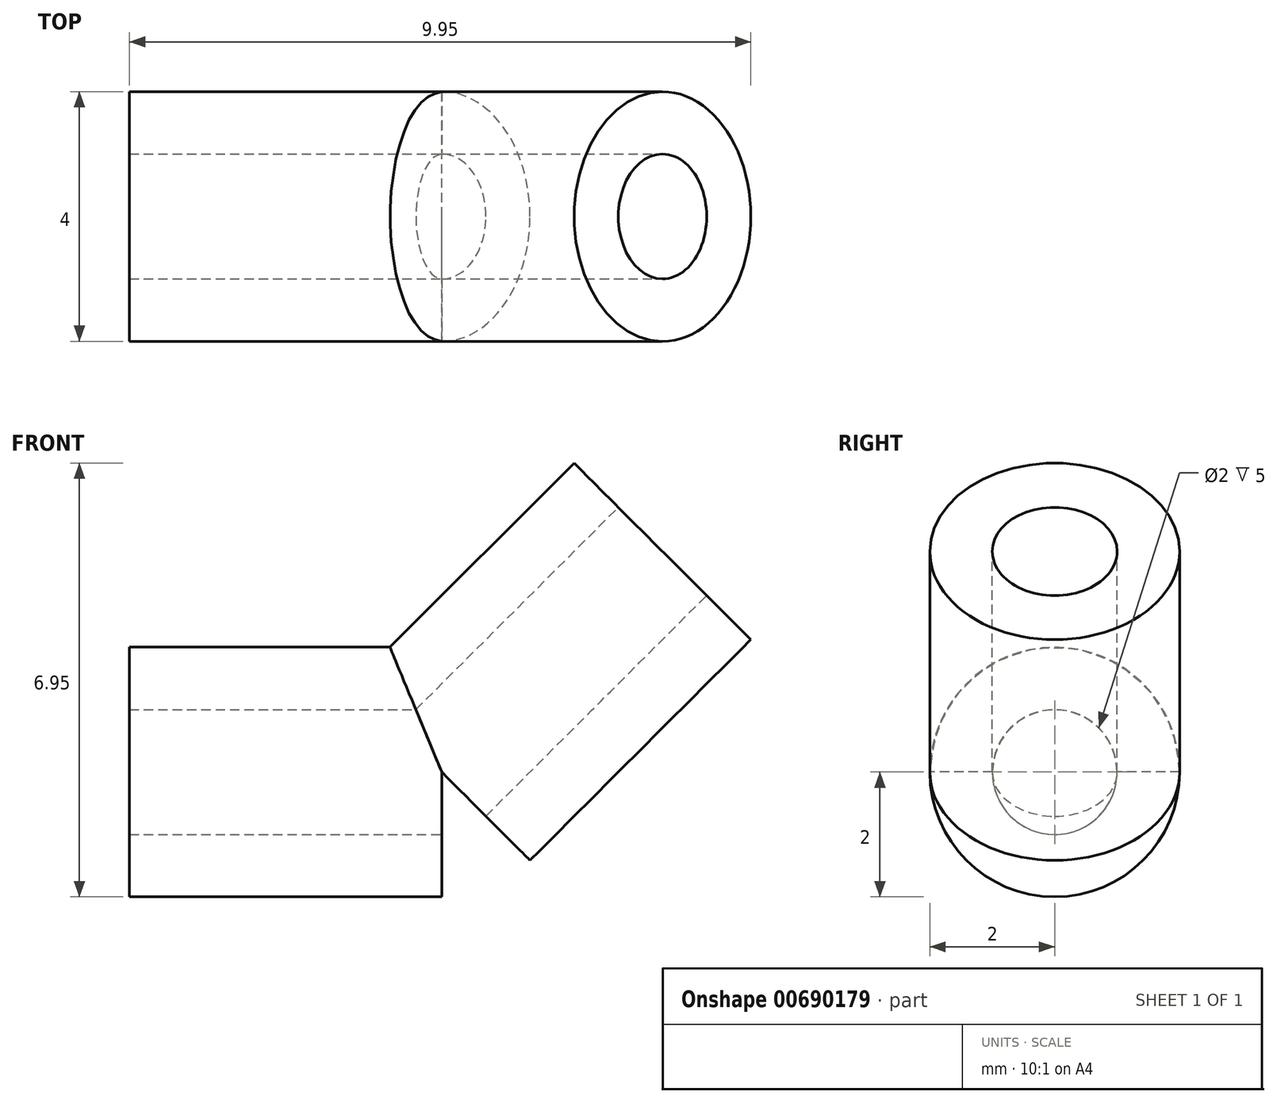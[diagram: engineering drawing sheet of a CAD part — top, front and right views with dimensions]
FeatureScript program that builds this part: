
annotation { "Feature Type Name" : "Feature", "Feature Type Description" : "" }
export const myFeature = defineFeature(function(context is Context, id is Id, definition is map)
    precondition{}
    {
        {
            var Q0;
            Q0=qCreatedBy(makeId("Front.planeOp"),FACE);
            var sketch = newSketch(context, id + "F0", { "sketchPlane" : qUnion([Q0])});
            skLineSegment(sketch, "E0", {"start": v(0, 0) * mm, "end": v(3.54, 3.54) * mm});
            skLineSegment(sketch, "E1", {"start": v(0, 0) * mm, "end": v(3.54, -3.54) * mm});
            skLineSegment(sketch, "E2", {"start": v(0, 0) * mm, "end": v(-5, 0) * mm});
            skSolve(sketch);
        }
        {
            var Q0;
            Q0=qCreatedBy(makeId("Right.planeOp"),FACE);
            var sketch = newSketch(context, id + "F1", { "sketchPlane" : qUnion([Q0])});
            skCircle(sketch, "E3", {"center": v(0, 0) * mm, "radius": 2 * mm});
            skCircle(sketch, "E4", {"center": v(0, 0) * mm, "radius": 1 * mm});
            skSolve(sketch);
        }
        {
            var Q0;
            Q0=makeQuery(id+"F1.imprint","IMPRINT",FACE,{"disambiguationData":[TD([[makeQuery(id+"F1.imprint","IMPRINT",EDGE,{"derivedFrom":sQuery(id+"F1.wireOp",EDGE,"E3")}),1.0]])]});
            extrude(context, id + "F2", {"entities" : qUnion([Q0]), "oppositeDirection" : true, "depth" : 5 * mm, "offsetDistance" : 25 * mm});
        }
        {
            var Q0;
            Q0=sQuery(id+"F0.wireOp",VERTEX,"E0.end");
            var Q1;
            Q1=sQuery(id+"F0.wireOp",EDGE,"E0");
            cPlane(context, id + "F3", {"entities" : qUnion([Q0, Q1]), "cplaneType" : CPlaneType.LINE_POINT, "offset" : 25 * mm, "width" : 150 * mm, "height" : 150 * mm});
        }
        {
            var Q0;
            Q0=qCreatedBy(id+"F3.planeOp",FACE);
            var sketch = newSketch(context, id + "F4", { "sketchPlane" : qUnion([Q0])});
            skCircle(sketch, "E5", {"center": v(0, 0) * mm, "radius": 1 * mm});
            skCircle(sketch, "E6", {"center": v(0, 0) * mm, "radius": 2 * mm});
            skSolve(sketch);
        }
        {
            var Q0;
            Q0=makeQuery(id+"F4.imprint","IMPRINT",FACE,{"disambiguationData":[TD([[makeQuery(id+"F4.imprint","IMPRINT",EDGE,{"derivedFrom":sQuery(id+"F4.wireOp",EDGE,"E5")}),-1.0]])]});
            extrude(context, id + "F5", {"entities" : qUnion([Q0]), "operationType" : NewBodyOperationType.ADD, "oppositeDirection" : true, "depth" : 5 * mm, "offsetDistance" : 25 * mm});
        }
        {
            var Q0;
            Q0=makeQuery(id+"F4.imprint","IMPRINT",FACE,{"disambiguationData":[TD([[makeQuery(id+"F4.imprint","IMPRINT",EDGE,{"derivedFrom":sQuery(id+"F4.wireOp",EDGE,"E5")}),1.0]])]});
            extrude(context, id + "F6", {"entities" : qUnion([Q0]), "operationType" : NewBodyOperationType.REMOVE, "oppositeDirection" : true, "depth" : 5 * mm, "offsetDistance" : 25 * mm});
        }
        {
            var Q0;
            Q0=makeQuery(id+"F1.imprint","IMPRINT",FACE,{"disambiguationData":[TD([[makeQuery(id+"F1.imprint","IMPRINT",EDGE,{"derivedFrom":sQuery(id+"F1.wireOp",EDGE,"E4")}),1.0]])]});
            extrude(context, id + "F7", {"entities" : qUnion([Q0]), "operationType" : NewBodyOperationType.REMOVE, "oppositeDirection" : true, "depth" : 5 * mm, "offsetDistance" : 25 * mm});
        }
    });
